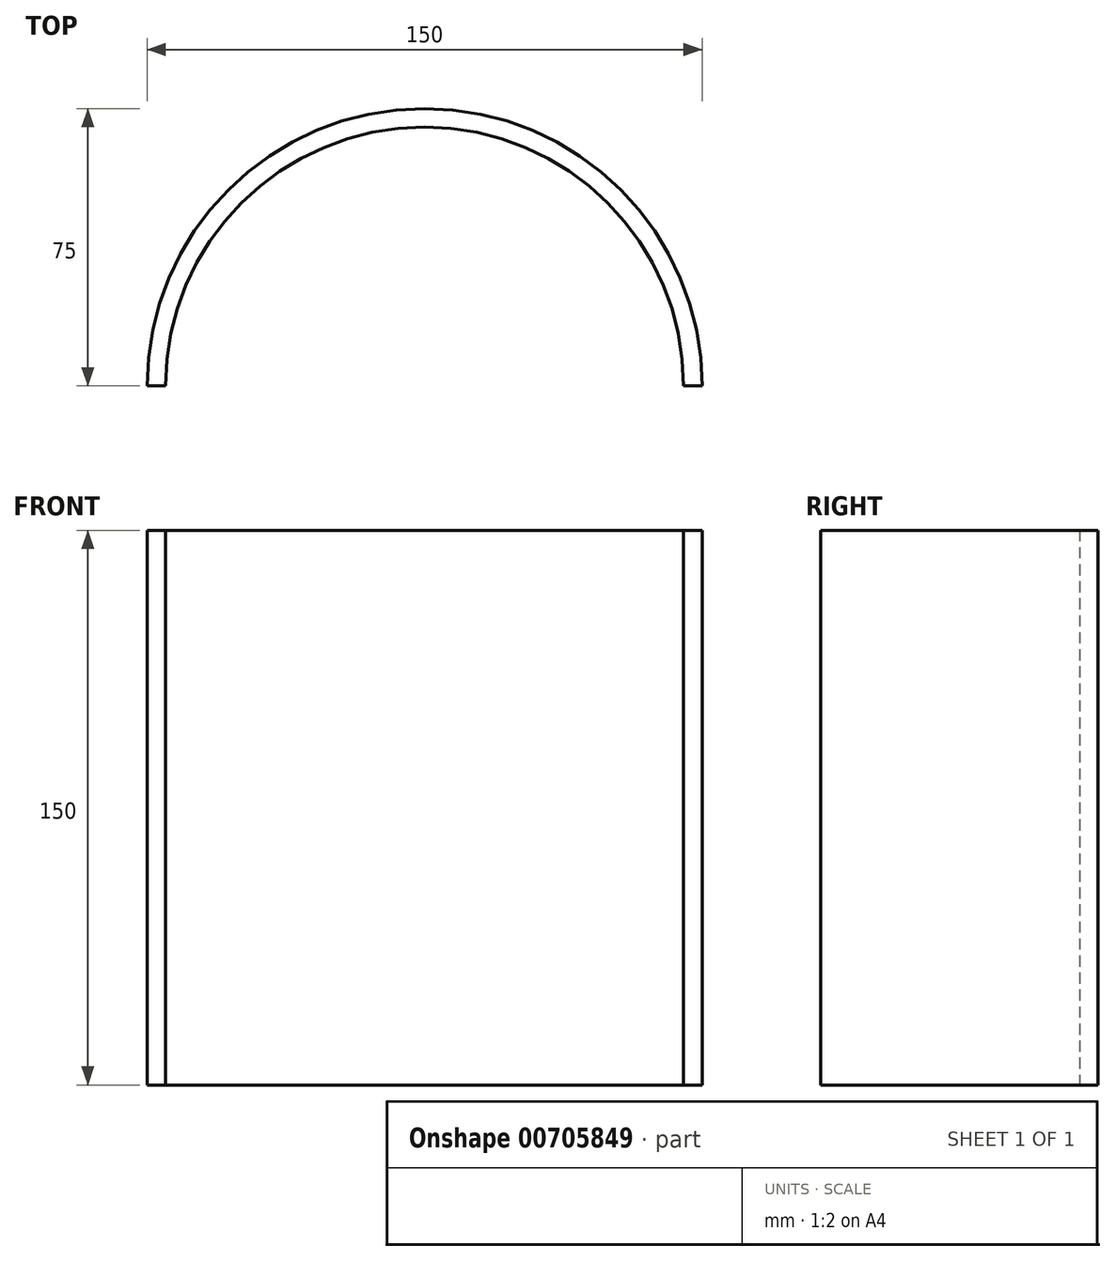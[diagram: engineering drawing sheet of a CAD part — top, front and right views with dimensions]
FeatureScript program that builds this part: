
annotation { "Feature Type Name" : "Feature", "Feature Type Description" : "" }
export const myFeature = defineFeature(function(context is Context, id is Id, definition is map)
    precondition{}
    {
        {
            var Q0;
            Q0=qCreatedBy(makeId("Top.planeOp"),FACE);
            var sketch = newSketch(context, id + "F0", { "sketchPlane" : qUnion([Q0])});
            skArc(sketch, "E0", {"start": v(-75, 0) * mm, "mid": v(0, 75) * mm, "end": v(75, 0) * mm});
            skArc(sketch, "E1", {"start": v(-70, 0) * mm, "mid": v(0, 70) * mm, "end": v(70, 0) * mm});
            skLineSegment(sketch, "E2", {"start": v(-75, 0) * mm, "end": v(-70, 0) * mm});
            skLineSegment(sketch, "E3", {"start": v(70, 0) * mm, "end": v(75, 0) * mm});
            skSolve(sketch);
        }
        {
            var Q0;
            Q0 = qSketchRegion(id + "F0", true);
            extrude(context, id + "F1", {"entities" : qUnion([Q0]), "depth" : 150 * mm, "offsetDistance" : 25 * mm});
        }
    });
